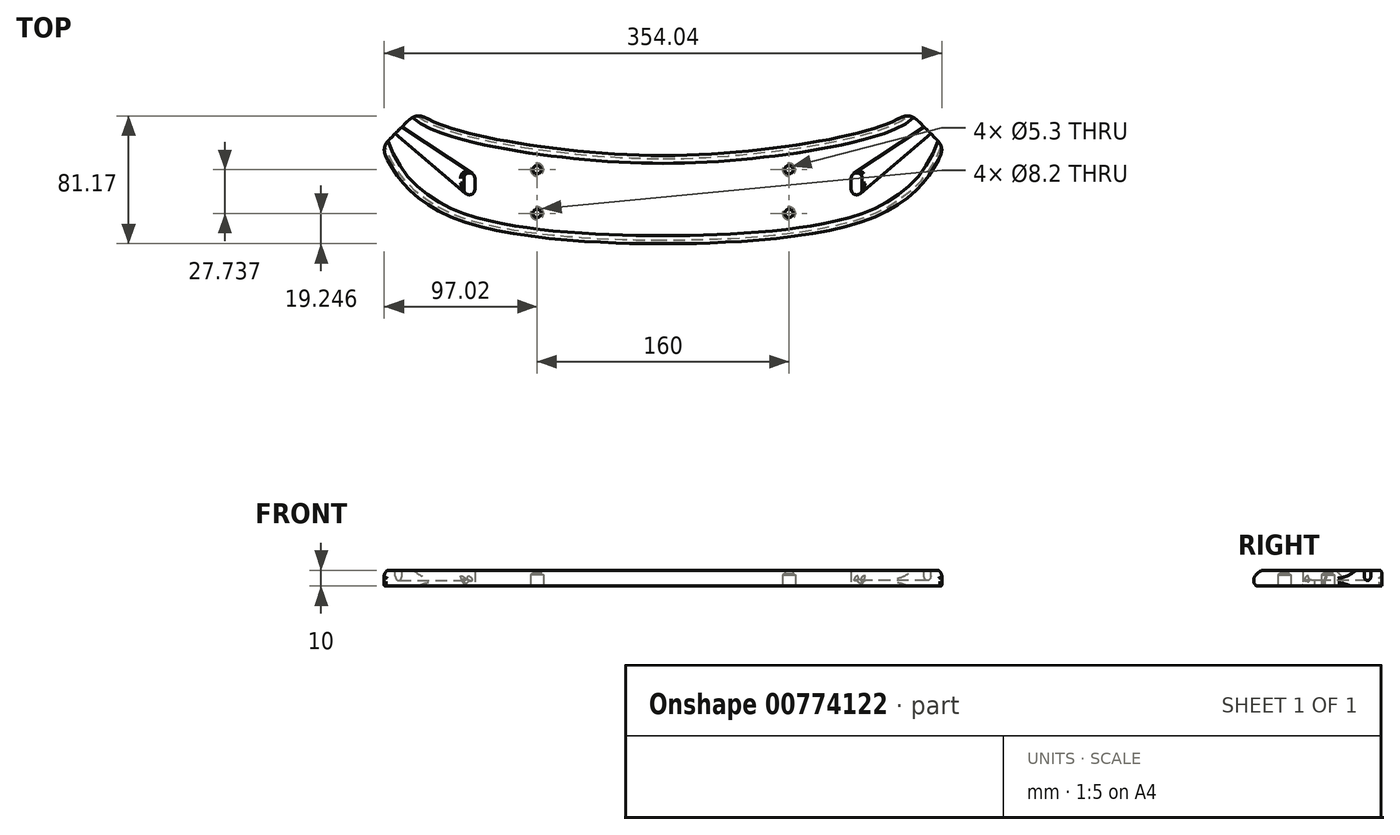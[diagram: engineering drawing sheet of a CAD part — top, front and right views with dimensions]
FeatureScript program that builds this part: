
annotation { "Feature Type Name" : "Feature", "Feature Type Description" : "" }
export const myFeature = defineFeature(function(context is Context, id is Id, definition is map)
    precondition{}
    {
        {
            var Q0;
            Q0=qCreatedBy(makeId("Top.planeOp"),FACE);
            var sketch = newSketch(context, id + "F0", { "sketchPlane" : qUnion([Q0])});
            skLineSegment(sketch, "E0", {"start": v(-123, 0) * mm, "end": v(123, 0) * mm, "construction": true});
            skLineSegment(sketch, "E1", {"start": v(0, 18) * mm, "end": v(0, -38) * mm});
            skLineSegment(sketch, "E2.bottom", {"start": v(126.5, -3.5) * mm, "end": v(126.5, 3.5) * mm});
            skLineSegment(sketch, "E2.top", {"start": v(119.5, -3.5) * mm, "end": v(119.5, 3.5) * mm});
            skLineSegment(sketch, "E2.left", {"start": v(126.5, -3.5) * mm, "end": v(119.5, -3.5) * mm, "construction": true});
            skLineSegment(sketch, "E2.right", {"start": v(126.5, 3.5) * mm, "end": v(119.5, 3.5) * mm, "construction": true});
            skPoint(sketch, "E2.middle", {"position": v(123, 0) * mm});
            skArc(sketch, "E3", {"start": v(119.5, -3.5) * mm, "mid": v(123, -7) * mm, "end": v(126.5, -3.5) * mm});
            skArc(sketch, "E4", {"start": v(126.5, 3.5) * mm, "mid": v(123, 7) * mm, "end": v(119.5, 3.5) * mm});
            skLineSegment(sketch, "E5", {"start": v(123, 30) * mm, "end": v(123, 0) * mm});
            skLineSegment(sketch, "E6", {"start": v(123, 0) * mm, "end": v(123, -26) * mm});
            skLineSegment(sketch, "E7", {"start": v(156, 46) * mm, "end": v(178.63, 23.37) * mm});
            skSolve(sketch);
        }
        {
            var Q0;
            Q0=qCreatedBy(makeId("Top.planeOp"),FACE);
            var sketch = newSketch(context, id + "F1", { "sketchPlane" : qUnion([Q0])});
            skLineSegment(sketch, "E8", {"start": v(0, 18) * mm, "end": v(0, -38) * mm});
            skLineSegment(sketch, "E9", {"start": v(156, 46) * mm, "end": v(178.63, 23.37) * mm});
            skFitSpline(sketch, "E10", {"points": [v(0, -38) * mm, v(128.3, -23.53) * mm, v(178.63, 23.37) * mm], "startDerivative": vector(45.02, 0) * mm, "endDerivative": vector(45.45, 116.98) * mm});
            skFitSpline(sketch, "E11", {"points": [v(0, 18) * mm, v(126.36, 32.9) * mm, v(156, 46) * mm], "startDerivative": vector(194.43, 0) * mm, "endDerivative": vector(37.46, 40) * mm});
            skLineSegment(sketch, "E12", {"start": v(0, 18) * mm, "end": v(-29.06, 18) * mm, "construction": true});
            skLineSegment(sketch, "E13", {"start": v(0, -38) * mm, "end": v(-26.25, -38) * mm, "construction": true});
            skLineSegment(sketch, "E14.0", {"start": v(126.5, -3.5) * mm, "end": v(126.5, 3.5) * mm});
            skArc(sketch, "E14.1", {"start": v(119.5, -3.5) * mm, "mid": v(123, -7) * mm, "end": v(126.5, -3.5) * mm});
            skLineSegment(sketch, "E14.2", {"start": v(119.5, -3.5) * mm, "end": v(119.5, 3.5) * mm});
            skArc(sketch, "E14.3", {"start": v(126.5, 3.5) * mm, "mid": v(123, 7) * mm, "end": v(119.5, 3.5) * mm});
            skSolve(sketch);
        }
        {
            var Q0;
            Q0 = qSketchRegion(id + "F1", true);
            extrude(context, id + "F2", {"entities" : qUnion([Q0]), "depth" : 10 * mm, "offsetDistance" : 25 * mm});
        }
        {
            var Q0;
            Q0=makeQuery(id+"F2.opExtrude","SWEPT_EDGE",EDGE,{"disambiguationData":[OSD([sQuery(id+"F1.wireOp",EDGE,"E9"),sQuery(id+"F1.wireOp",EDGE,"E10")])]});
            var Q1;
            Q1=makeQuery(id+"F2.opExtrude","SWEPT_EDGE",EDGE,{"disambiguationData":[OSD([sQuery(id+"F1.wireOp",EDGE,"E9"),sQuery(id+"F1.wireOp",EDGE,"E11")])]});
            fillet(context, id + "F3", {"entities" : qUnion([Q0, Q1]), "radius" : 12 * mm, "tangentPropagation" : true, "rho" : .6, "crossSection" : FilletCrossSection.CONIC, "allowEdgeOverflow" : false});
        }
        {
            var Q0;
            Q0=makeQuery(id+"F2.opExtrude","CAP_FACE",FACE,{"disambiguationData":[OSD([sQuery(id+"F1.wireOp",EDGE,"E8"),sQuery(id+"F1.wireOp",EDGE,"E9"),sQuery(id+"F1.wireOp",EDGE,"E10"),sQuery(id+"F1.wireOp",EDGE,"E11"),sQuery(id+"F1.wireOp",EDGE,"E14.0"),sQuery(id+"F1.wireOp",EDGE,"E14.1"),sQuery(id+"F1.wireOp",EDGE,"E14.2"),sQuery(id+"F1.wireOp",EDGE,"E14.3")])],"isStart":false});
            var sketch = newSketch(context, id + "F4", { "sketchPlane" : qUnion([Q0])});
            skLineSegment(sketch, "E15", {"start": v(165.82, 36.18) * mm, "end": v(121.06, 6.41) * mm});
            skLineSegment(sketch, "E16", {"start": v(170.06, 31.94) * mm, "end": v(125.27, -6.17) * mm});
            skLineSegment(sketch, "E17", {"start": v(165.82, 36.18) * mm, "end": v(170.06, 31.94) * mm});
            skPoint(sketch, "E18", {"position": v(167.94, 34.06) * mm});
            skLineSegment(sketch, "E19", {"start": v(121.06, 6.41) * mm, "end": v(125.27, -6.17) * mm});
            skSolve(sketch);
        }
        {
            var Q0;
            Q0 = qSketchRegion(id + "F4", true);
            extrude(context, id + "F5", {"entities" : qUnion([Q0]), "operationType" : NewBodyOperationType.REMOVE, "oppositeDirection" : true, "depth" : 6.5 * mm, "offsetDistance" : 25 * mm});
        }
        {
            var Q0;
            Q0=makeQuery(id+"F5.boolean.opBoolean","COPY",EDGE,{"derivedFrom":makeQuery(id+"F5.opExtrude","CAP_EDGE",EDGE,{"disambiguationData":[OSD([sQuery(id+"F4.wireOp",EDGE,"E15")])],"isStart":false})});
            var Q1;
            Q1=makeQuery(id+"F5.boolean.opBoolean","COPY",EDGE,{"derivedFrom":makeQuery(id+"F5.opExtrude","CAP_EDGE",EDGE,{"disambiguationData":[OSD([sQuery(id+"F4.wireOp",EDGE,"E16")])],"isStart":false})});
            fillet(context, id + "F6", {"entities" : qUnion([Q0, Q1]), "radius" : 3 * mm, "tangentPropagation" : true, "allowEdgeOverflow" : false});
        }
        {
            var Q0;
            Q0=makeQuery(id+"F5.boolean.opBoolean","INTERSECT",EDGE,{"derivedFrom":[makeQuery(id+"F2.opExtrude","SWEPT_FACE",FACE,{"disambiguationData":[OSD([sQuery(id+"F1.wireOp",EDGE,"E14.0")])]}),makeQuery(id+"F5.opExtrude","CAP_FACE",FACE,{"disambiguationData":[OSD([sQuery(id+"F4.wireOp",EDGE,"E15"),sQuery(id+"F4.wireOp",EDGE,"E16"),sQuery(id+"F4.wireOp",EDGE,"E17"),sQuery(id+"F4.wireOp",EDGE,"E19")])],"isStart":false})]});
            fillet(context, id + "F7", {"entities" : qUnion([Q0]), "radius" : 2 * mm, "tangentPropagation" : true, "rho" : .3, "defaultsChanged" : true, "vertexSettings" : [], "crossSection" : FilletCrossSection.CONIC, "allowEdgeOverflow" : false});
        }
        {
            var Q0;
            Q0=makeQuery(id+"F2.opExtrude","CAP_EDGE",EDGE,{"disambiguationData":[OSD([sQuery(id+"F1.wireOp",EDGE,"E14.3")])],"isStart":true});
            var Q1;
            Q1=makeQuery(id+"F5.boolean.opBoolean","COPY",EDGE,{"derivedFrom":makeQuery(id+"F5.opExtrude","SWEPT_EDGE",EDGE,{"disambiguationData":[OSD([sQuery(id+"F1.wireOp",EDGE,"E9"),sQuery(id+"F4.wireOp",EDGE,"E16"),sQuery(id+"F4.wireOp",EDGE,"E17")])]})});
            var Q2;
            Q2=makeQuery(id+"F5.boolean.opBoolean","COPY",EDGE,{"derivedFrom":makeQuery(id+"F5.opExtrude","SWEPT_EDGE",EDGE,{"disambiguationData":[OSD([sQuery(id+"F1.wireOp",EDGE,"E9"),sQuery(id+"F4.wireOp",EDGE,"E15"),sQuery(id+"F4.wireOp",EDGE,"E17")])]})});
            fillet(context, id + "F8", {"entities" : qUnion([Q0, Q1, Q2]), "radius" : 1 * mm, "tangentPropagation" : true, "rho" : .2, "crossSection" : FilletCrossSection.CONIC, "allowEdgeOverflow" : false});
        }
        {
            var Q0;
            Q0=makeQuery(id+"F2.opExtrude","CAP_FACE",FACE,{"disambiguationData":[OSD([sQuery(id+"F1.wireOp",EDGE,"E8"),sQuery(id+"F1.wireOp",EDGE,"E9"),sQuery(id+"F1.wireOp",EDGE,"E10"),sQuery(id+"F1.wireOp",EDGE,"E11"),sQuery(id+"F1.wireOp",EDGE,"E14.0"),sQuery(id+"F1.wireOp",EDGE,"E14.1"),sQuery(id+"F1.wireOp",EDGE,"E14.2"),sQuery(id+"F1.wireOp",EDGE,"E14.3")])],"isStart":true});
            var sketch = newSketch(context, id + "F9", { "sketchPlane" : qUnion([Q0])});
            skLineSegment(sketch, "E20", {"start": v(80, 33.75) * mm, "end": v(80, 18.75) * mm, "construction": true});
            skLineSegment(sketch, "E21", {"start": v(80, 18.75) * mm, "end": v(80, -8.98) * mm, "construction": true});
            skLineSegment(sketch, "E22", {"start": v(80, -8.98) * mm, "end": v(80, -23.98) * mm, "construction": true});
            skCircle(sketch, "E23", {"center": v(80, 18.75) * mm, "radius": 2.65 * mm});
            skCircle(sketch, "E24", {"center": v(80, -8.98) * mm, "radius": 2.65 * mm});
            skSolve(sketch);
        }
        {
            var Q0;
            Q0 = qSketchRegion(id + "F9", true);
            extrude(context, id + "F10", {"entities" : qUnion([Q0]), "operationType" : NewBodyOperationType.REMOVE, "endBound" : BoundingType.UP_TO_NEXT, "oppositeDirection" : true, "depth" : 25 * mm, "offsetDistance" : 25 * mm});
        }
        {
            var Q0;
            Q0=makeQuery(id+"F2.opExtrude","CAP_FACE",FACE,{"disambiguationData":[OSD([sQuery(id+"F1.wireOp",EDGE,"E8"),sQuery(id+"F1.wireOp",EDGE,"E9"),sQuery(id+"F1.wireOp",EDGE,"E10"),sQuery(id+"F1.wireOp",EDGE,"E11"),sQuery(id+"F1.wireOp",EDGE,"E14.0"),sQuery(id+"F1.wireOp",EDGE,"E14.1"),sQuery(id+"F1.wireOp",EDGE,"E14.2"),sQuery(id+"F1.wireOp",EDGE,"E14.3")])],"isStart":true});
            var sketch = newSketch(context, id + "F11", { "sketchPlane" : qUnion([Q0])});
            skCircle(sketch, "E25", {"center": v(80, -8.98) * mm, "radius": 4.1 * mm});
            skCircle(sketch, "E26", {"center": v(80, 18.75) * mm, "radius": 4.1 * mm});
            skSolve(sketch);
        }
        {
            var Q0;
            Q0 = qSketchRegion(id + "F11", true);
            var Q1;
            Q1 = qConstructionFilter(qBodyType(qCreatedBy(id + "F11" ,EDGE), BodyType.WIRE), ConstructionObject.NO);
            extrude(context, id + "F12", {"entities" : qUnion([Q0]), "operationType" : NewBodyOperationType.REMOVE, "surfaceEntities" : qUnion([Q1]), "oppositeDirection" : true, "depth" : 7 * mm, "offsetDistance" : 25 * mm});
        }
        {
            var Q0;
            Q0=makeQuery(id+"F12.boolean.opBoolean","INTERSECT",EDGE,{"derivedFrom":[makeQuery(id+"F10.boolean.opBoolean","COPY",FACE,{"derivedFrom":makeQuery(id+"F10.opExtrude","SWEPT_FACE",FACE,{"disambiguationData":[OSD([sQuery(id+"F9.wireOp",EDGE,"E23")])]})}),makeQuery(id+"F12.opExtrude","CAP_FACE",FACE,{"disambiguationData":[OSD([sQuery(id+"F11.wireOp",EDGE,"E26")])],"isStart":false})]});
            var Q1;
            Q1=makeQuery(id+"F12.boolean.opBoolean","INTERSECT",EDGE,{"derivedFrom":[makeQuery(id+"F10.boolean.opBoolean","COPY",FACE,{"derivedFrom":makeQuery(id+"F10.opExtrude","SWEPT_FACE",FACE,{"disambiguationData":[OSD([sQuery(id+"F9.wireOp",EDGE,"E24")])]})}),makeQuery(id+"F12.opExtrude","CAP_FACE",FACE,{"disambiguationData":[OSD([sQuery(id+"F11.wireOp",EDGE,"E25")])],"isStart":false})]});
            chamfer(context, id + "F13", {"entities" : qUnion([Q0, Q1]), "chamferType" : ChamferType.OFFSET_ANGLE, "width" : 1.5 * mm, "oppositeDirection" : false, "angle" : 30 * degree, "tangentPropagation" : true});
        }
        {
            var Q0;
            Q0=makeQuery(id+"F2.opExtrude","SWEPT_BODY",BODY,{"disambiguationData":[OSD([sQuery(id+"F1.wireOp",EDGE,"E8"),sQuery(id+"F1.wireOp",EDGE,"E9"),sQuery(id+"F1.wireOp",EDGE,"E10"),sQuery(id+"F1.wireOp",EDGE,"E11")])]});
            var Q1;
            Q1=makeQuery(id+"F2.opExtrude","SWEPT_FACE",FACE,{"disambiguationData":[OSD([sQuery(id+"F1.wireOp",EDGE,"E8")])]});
            mirror(context, id + "F14", {"operationType" : NewBodyOperationType.ADD, "entities" : qUnion([Q0]), "mirrorPlane" : qUnion([Q1])});
        }
        {
            var Q0;
            Q0=makeQuery(id+"F2.opExtrude","CAP_EDGE",EDGE,{"disambiguationData":[OSD([sQuery(id+"F1.wireOp",EDGE,"E11")])],"isStart":false});
            var Q1;
            Q1=makeQuery(id+"F2.opExtrude","CAP_EDGE",EDGE,{"disambiguationData":[OSD([sQuery(id+"F1.wireOp",EDGE,"E10")])],"isStart":false});
            var Q2;
            Q2=makeQuery(id+"F14.opPattern","COPY",EDGE,{"derivedFrom":makeQuery(id+"F2.opExtrude","CAP_EDGE",EDGE,{"disambiguationData":[OSD([sQuery(id+"F1.wireOp",EDGE,"E11")])],"isStart":false}),"instanceName":"1"});
            var Q3;
            Q3=makeQuery(id+"F14.opPattern","COPY",EDGE,{"derivedFrom":makeQuery(id+"F2.opExtrude","CAP_EDGE",EDGE,{"disambiguationData":[OSD([sQuery(id+"F1.wireOp",EDGE,"E10")])],"isStart":false}),"instanceName":"1"});
            fillet(context, id + "F15", {"entities" : qUnion([Q0, Q1, Q2, Q3]), "radius" : 5 * mm, "rho" : .2, "crossSection" : FilletCrossSection.CONIC, "allowEdgeOverflow" : false});
        }
        {
            var Q0;
            Q0=makeQuery(id+"F14.opPattern","COPY",EDGE,{"derivedFrom":makeQuery(id+"F2.opExtrude","CAP_EDGE",EDGE,{"disambiguationData":[OSD([sQuery(id+"F1.wireOp",EDGE,"E10")])],"isStart":true}),"instanceName":"1"});
            var Q1;
            Q1=makeQuery(id+"F2.opExtrude","CAP_EDGE",EDGE,{"disambiguationData":[OSD([sQuery(id+"F1.wireOp",EDGE,"E10")])],"isStart":true});
            var Q2;
            Q2=makeQuery(id+"F2.opExtrude","CAP_EDGE",EDGE,{"disambiguationData":[OSD([sQuery(id+"F1.wireOp",EDGE,"E11")])],"isStart":true});
            var Q3;
            Q3=makeQuery(id+"F14.opPattern","COPY",EDGE,{"derivedFrom":makeQuery(id+"F2.opExtrude","CAP_EDGE",EDGE,{"disambiguationData":[OSD([sQuery(id+"F1.wireOp",EDGE,"E11")])],"isStart":true}),"instanceName":"1"});
            fillet(context, id + "F16", {"entities" : qUnion([Q0, Q1, Q2, Q3]), "radius" : 2 * mm, "rho" : .2, "crossSection" : FilletCrossSection.CONIC, "allowEdgeOverflow" : false});
        }
    });
